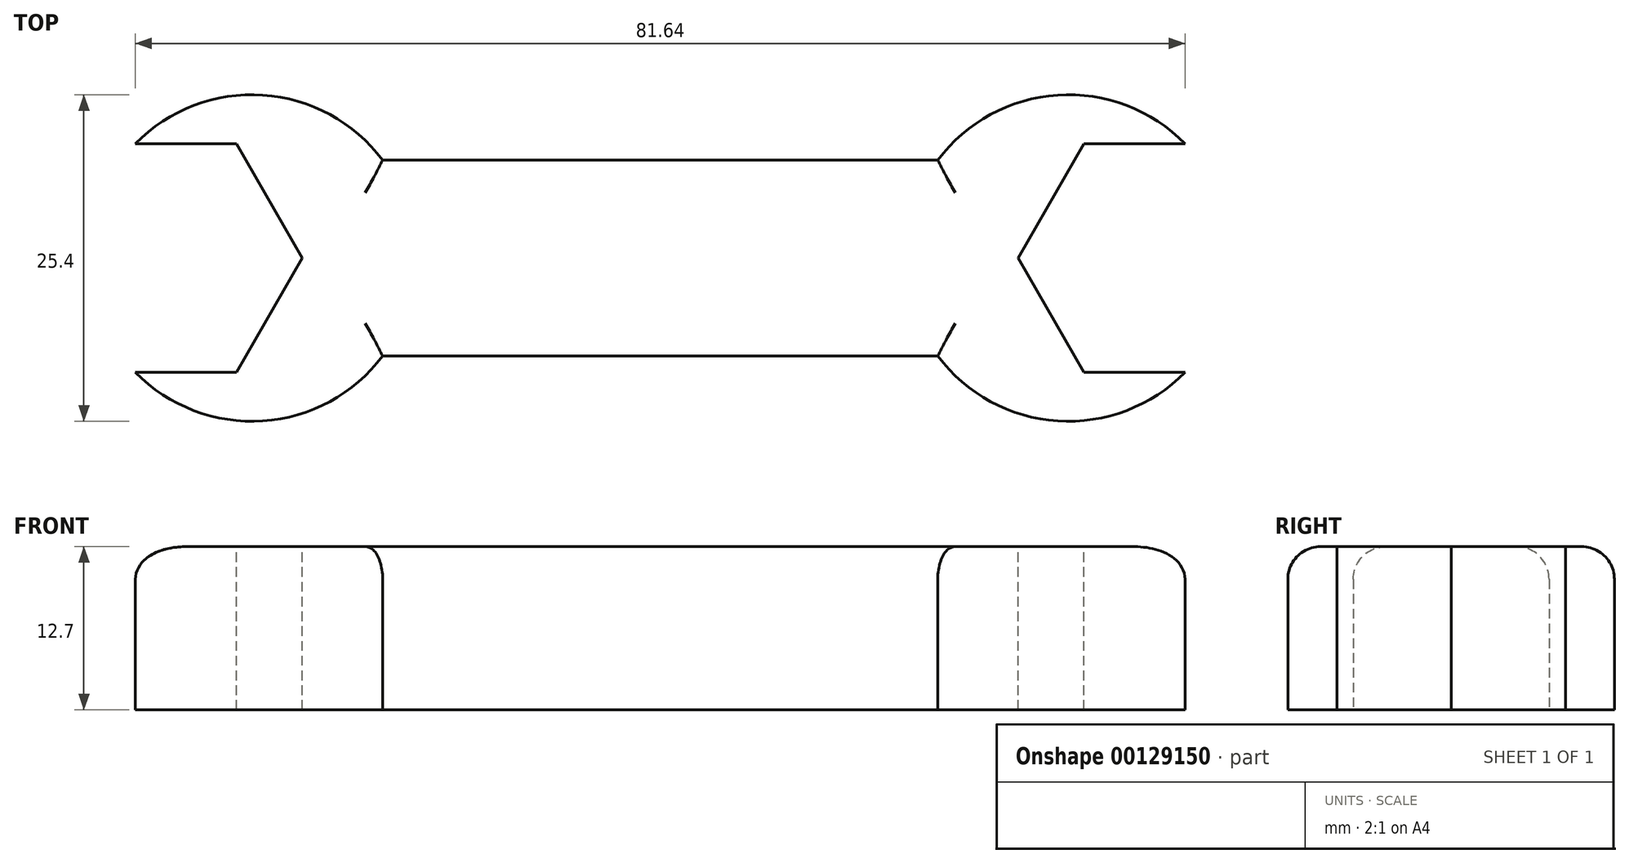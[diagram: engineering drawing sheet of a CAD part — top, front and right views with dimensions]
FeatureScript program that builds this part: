
annotation { "Feature Type Name" : "Feature", "Feature Type Description" : "" }
export const myFeature = defineFeature(function(context is Context, id is Id, definition is map)
    precondition{}
    {
        {
            var Q0;
            Q0=qCreatedBy(makeId("Top.planeOp"),FACE);
            var sketch = newSketch(context, id + "F0", { "sketchPlane" : qUnion([Q0])});
            skArc(sketch, "E0", {"start": v(-21.59, 7.62) * mm, "mid": v(-44.45, 0) * mm, "end": v(-21.59, -7.62) * mm});
            skArc(sketch, "E1", {"start": v(21.59, -7.62) * mm, "mid": v(44.45, 0) * mm, "end": v(21.59, 7.62) * mm});
            skLineSegment(sketch, "E2", {"start": v(-21.59, 7.62) * mm, "end": v(21.59, 7.62) * mm});
            skLineSegment(sketch, "E3", {"start": v(-21.6, -7.62) * mm, "end": v(21.59, -7.62) * mm});
            skLineSegment(sketch, "E4", {"start": v(-31.75, 0) * mm, "end": v(31.75, 0) * mm, "construction": true});
            skSolve(sketch);
        }
        {
            var Q0;
            Q0=makeQuery(id+"F0.imprint","IMPRINT",FACE,{"disambiguationData":[TD([[makeQuery(id+"F0.imprint","IMPRINT",EDGE,{"derivedFrom":sQuery(id+"F0.wireOp",EDGE,"E0")}),1.0]])]});
            extrude(context, id + "F1", {"entities" : qUnion([Q0]), "endBound" : BoundingType.SYMMETRIC, "depth" : 12.7 * mm});
        }
        {
            var Q0;
            Q0=makeQuery(id+"F1.opExtrude","CAP_FACE",FACE,{"disambiguationData":[OSD([sQuery(id+"F0.wireOp",EDGE,"E0"),sQuery(id+"F0.wireOp",EDGE,"E1"),sQuery(id+"F0.wireOp",EDGE,"E2"),sQuery(id+"F0.wireOp",EDGE,"E3")])],"isStart":false});
            var sketch = newSketch(context, id + "F2", { "sketchPlane" : qUnion([Q0])});
            skCircle(sketch, "E5.cCircle", {"center": v(-38.1, 0) * mm, "radius": 8.9 * mm, "construction": true});
            skLineSegment(sketch, "E5.0", {"start": v(-43.23, -8.9) * mm, "end": v(-48.37, 0) * mm});
            skLineSegment(sketch, "E5.1", {"start": v(-48.37, 0) * mm, "end": v(-43.23, 8.89) * mm});
            skLineSegment(sketch, "E5.2", {"start": v(-43.23, 8.89) * mm, "end": v(-32.97, 8.9) * mm});
            skLineSegment(sketch, "E5.3", {"start": v(-32.97, 8.9) * mm, "end": v(-27.83, 0) * mm});
            skLineSegment(sketch, "E5.4", {"start": v(-27.83, 0) * mm, "end": v(-32.97, -8.89) * mm});
            skLineSegment(sketch, "E5.5", {"start": v(-32.97, -8.89) * mm, "end": v(-43.23, -8.9) * mm});
            skPoint(sketch, "E5.0.midPoint", {"position": v(-45.8, -4.45) * mm});
            skPoint(sketch, "E6", {"position": v(-44.45, 0) * mm});
            skSolve(sketch);
        }
        {
            var Q0;
            Q0 = qSketchRegion(id + "F2", true);
            extrude(context, id + "F3", {"entities" : qUnion([Q0]), "endBound" : BoundingType.THROUGH_ALL, "oppositeDirection" : true, "depth" : 25.4 * mm});
        }
        {
            var Q0;
            Q0=makeQuery(id+"F3.opExtrude","SWEPT_BODY",BODY,{"disambiguationData":[OSD([sQuery(id+"F2.wireOp",EDGE,"E5.0"),sQuery(id+"F2.wireOp",EDGE,"E5.1"),sQuery(id+"F2.wireOp",EDGE,"E5.2"),sQuery(id+"F2.wireOp",EDGE,"E5.3"),sQuery(id+"F2.wireOp",EDGE,"E5.4"),sQuery(id+"F2.wireOp",EDGE,"E5.5")])]});
            var Q1;
            Q1=qCreatedBy(makeId("Right.planeOp"),FACE);
            mirror(context, id + "F4", {"operationType" : NewBodyOperationType.REMOVE, "entities" : qUnion([Q0]), "mirrorPlane" : qUnion([Q1])});
        }
        {
            var Q0;
            Q0=makeQuery(id+"F3.opExtrude","SWEPT_BODY",BODY,{"disambiguationData":[OSD([sQuery(id+"F2.wireOp",EDGE,"E5.0"),sQuery(id+"F2.wireOp",EDGE,"E5.1"),sQuery(id+"F2.wireOp",EDGE,"E5.2"),sQuery(id+"F2.wireOp",EDGE,"E5.3"),sQuery(id+"F2.wireOp",EDGE,"E5.4"),sQuery(id+"F2.wireOp",EDGE,"E5.5")])]});
            var Q1;
            Q1=makeQuery(id+"F1.opExtrude","SWEPT_BODY",BODY,{"disambiguationData":[OSD([sQuery(id+"F0.wireOp",EDGE,"E0"),sQuery(id+"F0.wireOp",EDGE,"E1"),sQuery(id+"F0.wireOp",EDGE,"E2"),sQuery(id+"F0.wireOp",EDGE,"E3")])]});
            booleanBodies(context, id + "F5", {"operationType" : BooleanOperationType.SUBTRACTION, "tools" : qUnion([Q0]), "targets" : qUnion([Q1])});
        }
        {
            var Q0;
            Q0=makeQuery(id+"F1.opExtrude","CAP_EDGE",EDGE,{"disambiguationData":[OSD([sQuery(id+"F0.wireOp",EDGE,"E3")])],"isStart":false});
            var Q1;
            {var subQ0=sQuery(id+"F0.wireOp",EDGE,"E0");var subQ1=sQuery(id+"F0.wireOp",EDGE,"E3");Q1=makeQuery(id+"F5.opBoolean","SPLIT",EDGE,{"disambiguationData":[TD([makeQuery(id+"F1.opExtrude","SWEPT_FACE",FACE,{"disambiguationData":[OSD([subQ1])]})])],"derivedFrom":makeQuery(id+"F1.opExtrude","CAP_EDGE",EDGE,{"disambiguationData":[OSD([subQ0])],"isStart":false})});}
            var Q2;
            {var subQ0=sQuery(id+"F0.wireOp",EDGE,"E0");var subQ1=sQuery(id+"F0.wireOp",EDGE,"E2");Q2=makeQuery(id+"F5.opBoolean","SPLIT",EDGE,{"disambiguationData":[TD([makeQuery(id+"F1.opExtrude","SWEPT_FACE",FACE,{"disambiguationData":[OSD([subQ1])]})])],"derivedFrom":makeQuery(id+"F1.opExtrude","CAP_EDGE",EDGE,{"disambiguationData":[OSD([subQ0])],"isStart":false})});}
            var Q3;
            Q3=makeQuery(id+"F1.opExtrude","CAP_EDGE",EDGE,{"disambiguationData":[OSD([sQuery(id+"F0.wireOp",EDGE,"E2")])],"isStart":false});
            var Q4;
            {var subQ0=sQuery(id+"F0.wireOp",EDGE,"E2");var subQ1=sQuery(id+"F0.wireOp",EDGE,"E1");Q4=makeQuery(id+"F4.boolean.opBoolean","SPLIT",EDGE,{"disambiguationData":[TD([makeQuery(id+"F1.opExtrude","SWEPT_FACE",FACE,{"disambiguationData":[OSD([subQ0])]})])],"derivedFrom":makeQuery(id+"F1.opExtrude","CAP_EDGE",EDGE,{"disambiguationData":[OSD([subQ1])],"isStart":false})});}
            var Q5;
            {var subQ0=sQuery(id+"F0.wireOp",EDGE,"E3");var subQ1=sQuery(id+"F0.wireOp",EDGE,"E1");Q5=makeQuery(id+"F4.boolean.opBoolean","SPLIT",EDGE,{"disambiguationData":[TD([makeQuery(id+"F1.opExtrude","SWEPT_FACE",FACE,{"disambiguationData":[OSD([subQ0])]})])],"derivedFrom":makeQuery(id+"F1.opExtrude","CAP_EDGE",EDGE,{"disambiguationData":[OSD([subQ1])],"isStart":false})});}
            fillet(context, id + "F6", {"entities" : qUnion([Q0, Q1, Q2, Q3, Q4, Q5]), "radius" : 2.54 * mm, "tangentPropagation" : true, "allowEdgeOverflow" : false});
        }
    });
